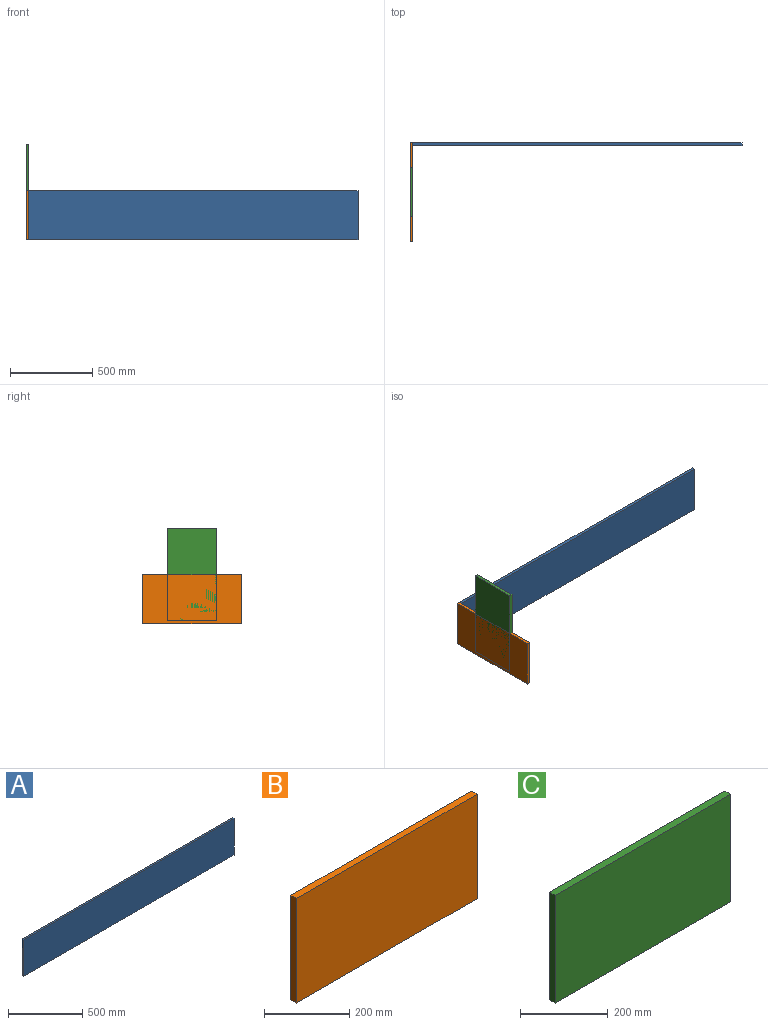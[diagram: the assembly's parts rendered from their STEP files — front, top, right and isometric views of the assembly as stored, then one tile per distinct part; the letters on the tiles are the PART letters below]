
ASSEMBLY  parts=3 mates=4
PART A: 6 faces, bbox 2000x18x300 mm
  f0: plane 300x18mm, normal (-1,0,0), area 5400mm2, adj f1,f3,f4,f5
  f1: plane 2000x18mm, normal (0,0,-1), area 36000mm2, adj f0,f2,f4,f5
  f2: plane 300x18mm, normal (1,0,0), area 5400mm2, adj f1,f3,f4,f5
  f3: plane 2000x18mm, normal (0,0,1), area 36000mm2, adj f0,f2,f4,f5
  f4: plane 2000x300mm, normal (0,-1,0), area 600000mm2, adj f0,f1,f2,f3
  f5: plane 2000x300mm, normal (0,1,0), area 600000mm2, adj f0,f1,f2,f3
PART B: 6 faces, bbox 600x18x300 mm
  f0: plane 300x18mm, normal (-1,0,0), area 5400mm2, adj f1,f3,f4,f5
  f1: plane 600x18mm, normal (0,0,-1), area 10800mm2, adj f0,f2,f4,f5
  f2: plane 300x18mm, normal (1,0,0), area 5400mm2, adj f1,f3,f4,f5
  f3: plane 600x18mm, normal (0,0,1), area 10800mm2, adj f0,f2,f4,f5
  f4: plane 600x300mm, normal (0,-1,0), area 180000mm2, adj f0,f1,f2,f3
  f5: plane 600x300mm, normal (0,1,0), area 180000mm2, adj f0,f1,f2,f3
PART C: 6 faces, bbox 564x18x300 mm
  f0: plane 300x18mm, normal (-1,0,0), area 5400mm2, adj f1,f3,f4,f5
  f1: plane 564x18mm, normal (0,0,-1), area 10152mm2, adj f0,f2,f4,f5
  f2: plane 300x18mm, normal (1,0,0), area 5400mm2, adj f1,f3,f4,f5
  f3: plane 564x18mm, normal (0,0,1), area 10152mm2, adj f0,f2,f4,f5
  f4: plane 564x300mm, normal (0,-1,0), area 169200mm2, adj f0,f1,f2,f3
  f5: plane 564x300mm, normal (0,1,0), area 169200mm2, adj f0,f1,f2,f3
PLACE A at identity
PLACE B rot(axis=(0,0,1),90deg) t=(-18,-600,0)mm
PLACE C rot(axis=(0.58,0.58,-0.58),120deg) t=(0,-150,582)mm
MATE parallel C.f5 <-> B.f4  axis (1,0,0) through (0,-300,300)mm
MATE planar A.f5 <-> B.f2  axis (0,1,0) through (1000,0,150)mm
MATE planar A.f0 <-> B.f4  axis (-1,0,0) through (0,-9,150)mm
MATE planar B.f1 <-> A.f1  axis (0,0,-1) through (-9,-300,0)mm
